# Revit family: Tyco_Valve_CV_1FR_GxG_2inch_595901020_Native
name_source: partatom
category: Pipe Accessories
revit_build: Autodesk Revit 2016 (Build: 20150220_1215(x64)
units: mm (PartAtom-declared; Revit-internal decimal feet)

## family parameters
Always vertical = Yes
Cut with Voids When Loaded = No
OmniClass Number = 23.65.55.14.17
OmniClass Title = Adjusting/Controlling Valves for Liquid Services
Part Type = Valve - Breaks Into
Round Connector Dimension = Use Diameter
Shared = No
Work Plane-Based = No

## types (1)
- Tyco_Valve_CV_1FR_GxG_2inch_595901020_Native
    COBie = Yes
    COBie.Component.Description = Riser Swing Check GxG TFP 950 CV-1FR 2 (Gmc)
    COBie.Component.Name = Valves:Riser Swing Check GxG
    COBie.Type = Yes
    COBie.Type.AssetType = Fixed
    COBie.Type.Category = Pr_65_54_95_97:Valves
    COBie.Type.Finish = non-lead paint
    COBie.Type.Manufacturer = Tyco Fire Protection Products
    COBie.Type.Material = Ductile Iron
    COBie.Type.ModelNumber = 595901020
    COBie.Type.ModelReference = Swing Riser Check GxG TFP 950 CV-1FR 2 (Gmc)
    COBie.Type.NominalHeight = 0' - 0"
    COBie.Type.NominalLength = 0' - 0"
    COBie.Type.NominalWidth = 0' - 0"
    COBie.Type.ReplacementCost = 0 $
    COBie.Type.Size = 2"(DN50) x 2"(DN50)
    COBie.Type.WarrantyGuarantorParts = http://tycofsbp.com
    Description = Model CV-1F Riser Swing Check valve 2" (DN50) with G x G
    Finish_ = Tyco - Red
    Flange Diameter 1 = 0"
    Flange Diameter 2 = 0"
    Length X = 7"
    Length Y = 0"
    Manufacturer = Tyco Fire Protection Products
    Manufacturer URL = www.tyco-fire.com
    Material_ = Ductile Iron
    Model = Riser Swing Check GxG
    Nominal Diameter 1 = 2"
    Nominal Diameter 2 = 2"
    Outside Diameter 1 = 2"
    Outside Diameter 2 = 2"
    Part No = 595901020
    Style Id = 0
    Takeout 1 = 0"
    Takeout 2 = 0"
    Technical Data Sheet No = TFP950

## geometry (parser evidence)
native form markers: Blend x2, Sweep x110
no freeform markers — native parametric forms only
